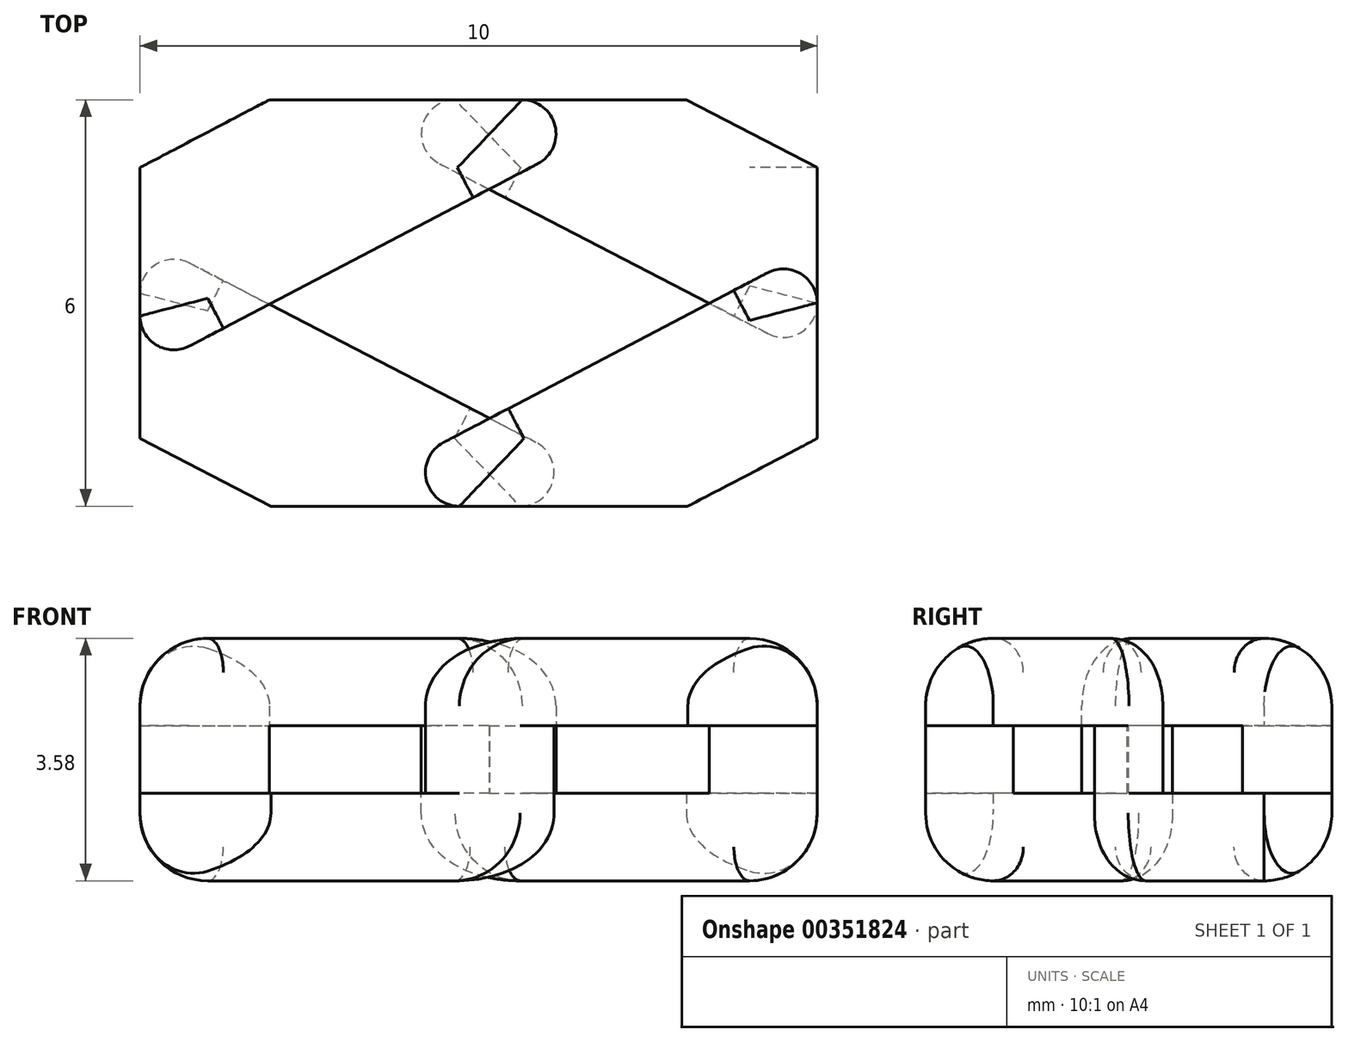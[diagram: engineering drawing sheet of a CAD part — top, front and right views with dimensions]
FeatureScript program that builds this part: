
annotation { "Feature Type Name" : "Feature", "Feature Type Description" : "" }
export const myFeature = defineFeature(function(context is Context, id is Id, definition is map)
    precondition{}
    {
        {
            var Q0;
            Q0=qCreatedBy(makeId("Front.planeOp"),FACE);
            var sketch = newSketch(context, id + "F0", { "sketchPlane" : qUnion([Q0])});
            skLineSegment(sketch, "E0.bottom", {"start": v(-10, 1.8) * mm, "end": v(0, 1.8) * mm});
            skLineSegment(sketch, "E0.top", {"start": v(-10, -1.8) * mm, "end": v(0, -1.8) * mm});
            skLineSegment(sketch, "E0.left", {"start": v(-10, 1.8) * mm, "end": v(-10, -1.8) * mm});
            skLineSegment(sketch, "E0.right", {"start": v(0, 1.8) * mm, "end": v(0, -1.8) * mm});
            skSolve(sketch);
        }
        {
            var Q0;
            Q0 = qSketchRegion(id + "F0", true);
            extrude(context, id + "F1", {"entities" : qUnion([Q0]), "depth" : 6 * mm});
        }
        {
            var Q0;
            Q0=makeQuery(id+"F1.opExtrude","CAP_EDGE",EDGE,{"disambiguationData":[OSD([sQuery(id+"F0.wireOp",EDGE,"E0.left")])],"isStart":false});
            var Q1;
            Q1=makeQuery(id+"F1.opExtrude","CAP_EDGE",EDGE,{"disambiguationData":[OSD([sQuery(id+"F0.wireOp",EDGE,"E0.bottom")])],"isStart":false});
            var Q2;
            Q2=makeQuery(id+"F1.opExtrude","CAP_EDGE",EDGE,{"disambiguationData":[OSD([sQuery(id+"F0.wireOp",EDGE,"E0.top")])],"isStart":false});
            var Q3;
            Q3=makeQuery(id+"F1.opExtrude","CAP_EDGE",EDGE,{"disambiguationData":[OSD([sQuery(id+"F0.wireOp",EDGE,"E0.right")])],"isStart":false});
            var Q4;
            Q4=makeQuery(id+"F1.opExtrude","SWEPT_EDGE",EDGE,{"disambiguationData":[OSD([sQuery(id+"F0.wireOp",EDGE,"E0.bottom"),sQuery(id+"F0.wireOp",EDGE,"E0.right")])]});
            var Q5;
            Q5=makeQuery(id+"F1.opExtrude","SWEPT_EDGE",EDGE,{"disambiguationData":[OSD([sQuery(id+"F0.wireOp",EDGE,"E0.bottom"),sQuery(id+"F0.wireOp",EDGE,"E0.left")])]});
            var Q6;
            Q6=makeQuery(id+"F1.opExtrude","CAP_EDGE",EDGE,{"disambiguationData":[OSD([sQuery(id+"F0.wireOp",EDGE,"E0.bottom")])],"isStart":true});
            var Q7;
            Q7=makeQuery(id+"F1.opExtrude","CAP_EDGE",EDGE,{"disambiguationData":[OSD([sQuery(id+"F0.wireOp",EDGE,"E0.left")])],"isStart":true});
            var Q8;
            Q8=makeQuery(id+"F1.opExtrude","CAP_EDGE",EDGE,{"disambiguationData":[OSD([sQuery(id+"F0.wireOp",EDGE,"E0.right")])],"isStart":true});
            var Q9;
            Q9=makeQuery(id+"F1.opExtrude","SWEPT_EDGE",EDGE,{"disambiguationData":[OSD([sQuery(id+"F0.wireOp",EDGE,"E0.top"),sQuery(id+"F0.wireOp",EDGE,"E0.right")])]});
            var Q10;
            Q10=makeQuery(id+"F1.opExtrude","CAP_EDGE",EDGE,{"disambiguationData":[OSD([sQuery(id+"F0.wireOp",EDGE,"E0.top")])],"isStart":true});
            var Q11;
            Q11=makeQuery(id+"F1.opExtrude","SWEPT_EDGE",EDGE,{"disambiguationData":[OSD([sQuery(id+"F0.wireOp",EDGE,"E0.top"),sQuery(id+"F0.wireOp",EDGE,"E0.left")])]});
            fillet(context, id + "F2", {"entities" : qUnion([Q0, Q1, Q2, Q3, Q4, Q5, Q6, Q7, Q8, Q9, Q10, Q11]), "radius" : 1 * mm, "tangentPropagation" : true, "allowEdgeOverflow" : false});
        }
        {
            var Q0;
            Q0=qCreatedBy(makeId("Top.planeOp"),FACE);
            cPlane(context, id + "F3", {"entities" : qUnion([Q0]), "cplaneType" : CPlaneType.OFFSET, "offset" : 25 * mm, "width" : 150 * mm, "height" : 150 * mm});
        }
        {
            var Q0;
            Q0=qCreatedBy(id+"F3.planeOp",FACE);
            var sketch = newSketch(context, id + "F4", { "sketchPlane" : qUnion([Q0])});
            skLineSegment(sketch, "E1", {"start": v(-42.94, -21.26) * mm, "end": v(1.72, 2.12) * mm});
            skLineSegment(sketch, "E2", {"start": v(1.72, 2.12) * mm, "end": v(3.11, -0.54) * mm});
            skLineSegment(sketch, "E3", {"start": v(3.11, -0.54) * mm, "end": v(-41.55, -23.92) * mm});
            skLineSegment(sketch, "E4", {"start": v(-41.55, -23.92) * mm, "end": v(-42.94, -21.26) * mm});
            skLineSegment(sketch, "E5", {"start": v(-1, -1) * mm, "end": v(-8.64, -5) * mm, "construction": true});
            skLineSegment(sketch, "E6", {"start": v(-47.97, -17.16) * mm, "end": v(-7.36, 4.1) * mm});
            skLineSegment(sketch, "E7", {"start": v(-5.84, 1.18) * mm, "end": v(-7.36, 4.1) * mm});
            skLineSegment(sketch, "E8", {"start": v(-5.84, 1.18) * mm, "end": v(-44.43, -19.02) * mm});
            skLineSegment(sketch, "E9", {"start": v(-47.97, -17.16) * mm, "end": v(-44.43, -19.02) * mm});
            skLineSegment(sketch, "E10", {"start": v(-36.2, -23.95) * mm, "end": v(1.9, -4) * mm});
            skLineSegment(sketch, "E11", {"start": v(1.9, -4) * mm, "end": v(5.08, -8.17) * mm});
            skLineSegment(sketch, "E12", {"start": v(5.08, -8.17) * mm, "end": v(-33.92, -28.58) * mm});
            skLineSegment(sketch, "E13", {"start": v(-33.92, -28.58) * mm, "end": v(-36.2, -23.95) * mm});
            skSolve(sketch);
        }
        {
            var Q0;
            Q0 = qSketchRegion(id + "F4", true);
            extrude(context, id + "F5", {"entities" : qUnion([Q0]), "operationType" : NewBodyOperationType.REMOVE, "oppositeDirection" : true, "depth" : 25.5 * mm});
        }
        {
            var Q0;
            Q0=qCreatedBy(makeId("Top.planeOp"),FACE);
            cPlane(context, id + "F6", {"entities" : qUnion([Q0]), "cplaneType" : CPlaneType.OFFSET, "offset" : 25 * mm, "oppositeDirection" : true, "width" : 150 * mm, "height" : 150 * mm});
        }
        {
            var Q0;
            Q0=qCreatedBy(id+"F6.planeOp",FACE);
            var sketch = newSketch(context, id + "F7", { "sketchPlane" : qUnion([Q0])});
            skLineSegment(sketch, "E14", {"start": v(-8.9, -0.9) * mm, "end": v(-1, -5) * mm, "construction": true});
            skLineSegment(sketch, "E15", {"start": v(-17.03, 1.6) * mm, "end": v(0.17, -7.3) * mm});
            skLineSegment(sketch, "E16", {"start": v(-17.03, 1.6) * mm, "end": v(-15.65, 4.27) * mm});
            skLineSegment(sketch, "E17", {"start": v(1.55, -4.63) * mm, "end": v(-15.65, 4.27) * mm});
            skLineSegment(sketch, "E18", {"start": v(1.55, -4.63) * mm, "end": v(0.17, -7.3) * mm});
            skLineSegment(sketch, "E19", {"start": v(-15.3, -2.26) * mm, "end": v(-3.02, -8.6) * mm});
            skLineSegment(sketch, "E20", {"start": v(-3.02, -8.6) * mm, "end": v(-4.8, -12.05) * mm});
            skLineSegment(sketch, "E21", {"start": v(-4.8, -12.05) * mm, "end": v(-16.97, -5.76) * mm});
            skLineSegment(sketch, "E22", {"start": v(-16.97, -5.76) * mm, "end": v(-15.3, -2.26) * mm});
            skLineSegment(sketch, "E23", {"start": v(-1.46, 7.83) * mm, "end": v(6.06, 3.94) * mm});
            skLineSegment(sketch, "E24", {"start": v(2.76, -2.43) * mm, "end": v(6.06, 3.94) * mm});
            skLineSegment(sketch, "E25", {"start": v(2.76, -2.43) * mm, "end": v(-5.9, 2.05) * mm});
            skLineSegment(sketch, "E26", {"start": v(-1.46, 7.83) * mm, "end": v(-5.9, 2.05) * mm});
            skSolve(sketch);
        }
        {
            var Q0;
            Q0 = qSketchRegion(id + "F7", true);
            extrude(context, id + "F8", {"entities" : qUnion([Q0]), "operationType" : NewBodyOperationType.REMOVE, "depth" : 25.5 * mm});
        }
        {
            var Q0;
            Q0=makeQuery(id+"F8.boolean.opBoolean","INTERSECT",EDGE,{"derivedFrom":[makeQuery(id+"F1.opExtrude","SWEPT_FACE",FACE,{"disambiguationData":[OSD([sQuery(id+"F0.wireOp",EDGE,"E0.top")])]}),makeQuery(id+"F8.opExtrude","SWEPT_FACE",FACE,{"disambiguationData":[OSD([sQuery(id+"F7.wireOp",EDGE,"E15")])]})]});
            var Q1;
            Q1=makeQuery(id+"F8.boolean.opBoolean","INTERSECT",EDGE,{"derivedFrom":[makeQuery(id+"F1.opExtrude","SWEPT_FACE",FACE,{"disambiguationData":[OSD([sQuery(id+"F0.wireOp",EDGE,"E0.top")])]}),makeQuery(id+"F8.opExtrude","SWEPT_FACE",FACE,{"disambiguationData":[OSD([sQuery(id+"F7.wireOp",EDGE,"E17")])]})]});
            var Q2;
            Q2=makeQuery(id+"F5.boolean.opBoolean","INTERSECT",EDGE,{"derivedFrom":[makeQuery(id+"F1.opExtrude","SWEPT_FACE",FACE,{"disambiguationData":[OSD([sQuery(id+"F0.wireOp",EDGE,"E0.bottom")])]}),makeQuery(id+"F5.opExtrude","SWEPT_FACE",FACE,{"disambiguationData":[OSD([sQuery(id+"F4.wireOp",EDGE,"E1")])]})]});
            var Q3;
            Q3=makeQuery(id+"F5.boolean.opBoolean","INTERSECT",EDGE,{"derivedFrom":[makeQuery(id+"F1.opExtrude","SWEPT_FACE",FACE,{"disambiguationData":[OSD([sQuery(id+"F0.wireOp",EDGE,"E0.bottom")])]}),makeQuery(id+"F5.opExtrude","SWEPT_FACE",FACE,{"disambiguationData":[OSD([sQuery(id+"F4.wireOp",EDGE,"E3")])]})]});
            fillet(context, id + "F9", {"entities" : qUnion([Q0, Q1, Q2, Q3]), "radius" : .5 * mm, "tangentPropagation" : true, "allowEdgeOverflow" : false});
        }
    });
